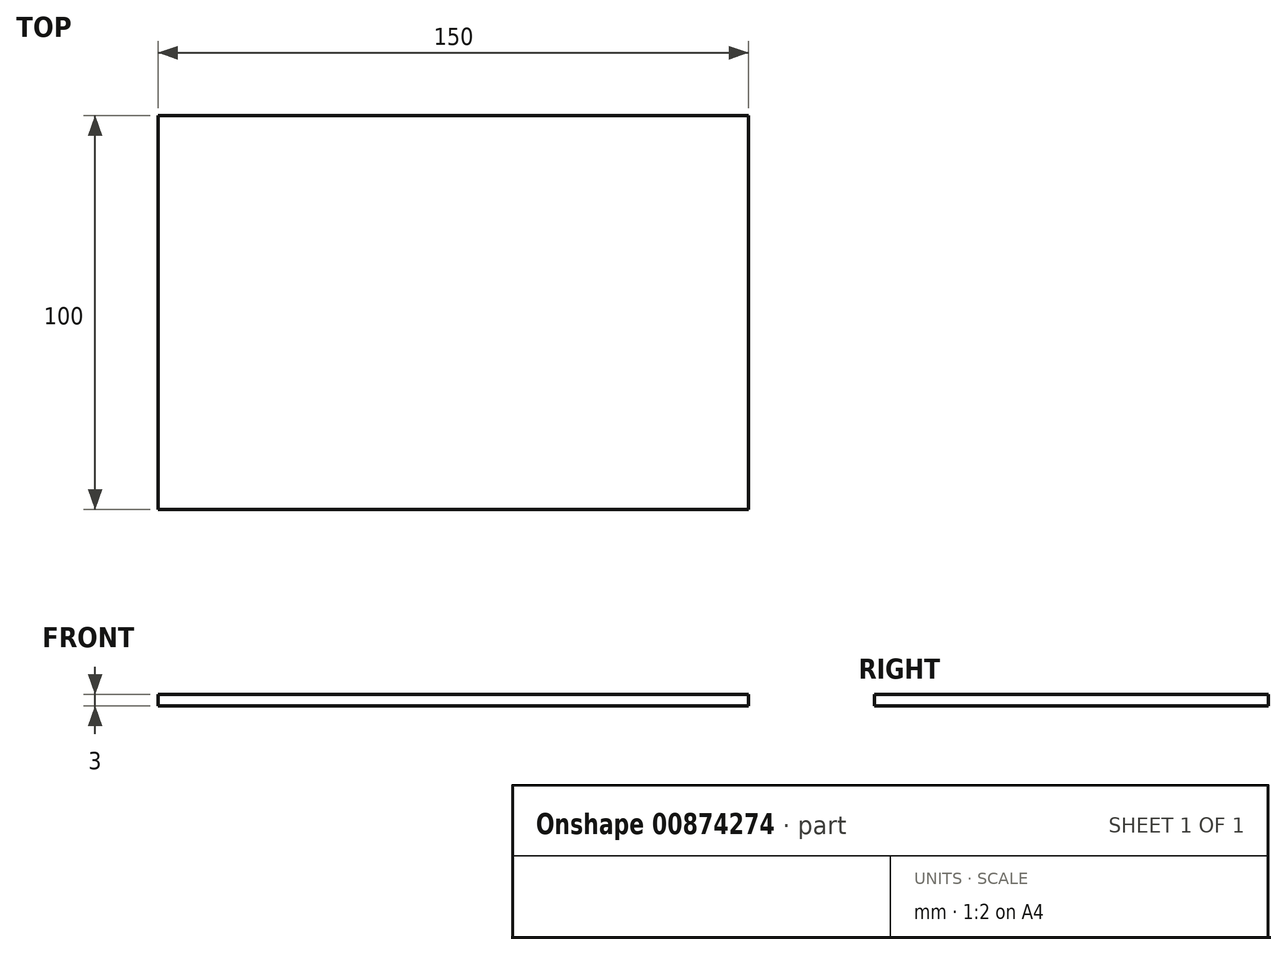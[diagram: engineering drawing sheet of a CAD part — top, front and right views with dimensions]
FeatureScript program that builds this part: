
annotation { "Feature Type Name" : "Feature", "Feature Type Description" : "" }
export const myFeature = defineFeature(function(context is Context, id is Id, definition is map)
    precondition{}
    {
        {
            var Q0;
            Q0=qCreatedBy(makeId("Top.planeOp"),FACE);
            var sketch = newSketch(context, id + "F0", { "sketchPlane" : qUnion([Q0])});
            skLineSegment(sketch, "E0.bottom", {"start": v(75, -50) * mm, "end": v(-75, -50) * mm});
            skLineSegment(sketch, "E0.top", {"start": v(75, 50) * mm, "end": v(-75, 50) * mm});
            skLineSegment(sketch, "E0.left", {"start": v(75, -50) * mm, "end": v(75, 50) * mm});
            skLineSegment(sketch, "E0.right", {"start": v(-75, -50) * mm, "end": v(-75, 50) * mm});
            skPoint(sketch, "E0.middle", {"position": v(0, 0) * mm});
            skSolve(sketch);
        }
        {
            var Q0;
            Q0 = qSketchRegion(id + "F0", true);
            extrude(context, id + "F1", {"entities" : qUnion([Q0]), "depth" : 3 * mm, "offsetDistance" : 25 * mm});
        }
    });
